# Revit family: O75401001_Lavamanos Vento
name_source: partatom
category: Plumbing Fixtures
units: mm (PartAtom-declared; Revit-internal decimal feet)

## family parameters
Cut with Voids When Loaded = No
Host = Face
OmniClass Number = 23.31.13.11
OmniClass Title = Single Sinks
Part Type = Normal
Room Calculation Point = No
Round Connector Dimension = Use Diameter
Shared = No

## types (1)
- O75401001_Lavamanos Vento
    Alto = 116 mm  [stored 0.380577 ft]
    Ancho = 420 mm  [stored 1.37795 ft]
    Creado por = BIMBAU
    Default Elevation = 1219 mm
    Description = Un lavamanos diseñado para espacios innovadores gracias a sus líneas simples y modernas con material de porcelana sanitaria. Es un vessel redondo, cónico y disponible en colores blanco y bone; además, permite instalar con grifería a la pared o en el mesón.
    Dimension del Pozo = 37.50 cm
    Fecha de creación = 07/04/2021
    Garantía = Garantía Integral de por vida.
    Manufacturer = Corona
    Material = Corona_Porcelana_Sanitaria
    Material 2 = Corona_Acero inoxidable
    Model = Vento
    Normatividad = ASME/ANSI A 112.19.2.
    Peso = 5 kg
    Profundidad = 420 mm  [stored 1.37795 ft]
    Profundidad del Pozo = 11.6 cm
    Referencia = O75401001
    Tipo de instalación = A pared
    URL = https://corona.co
    Uso = Redidencial

note: [stored X ft] marks values corroborated as IEEE doubles in the binary element streams (Revit-internal decimal feet)

## geometry (parser evidence)
native form markers: Sweep x7
no freeform markers — native parametric forms only
